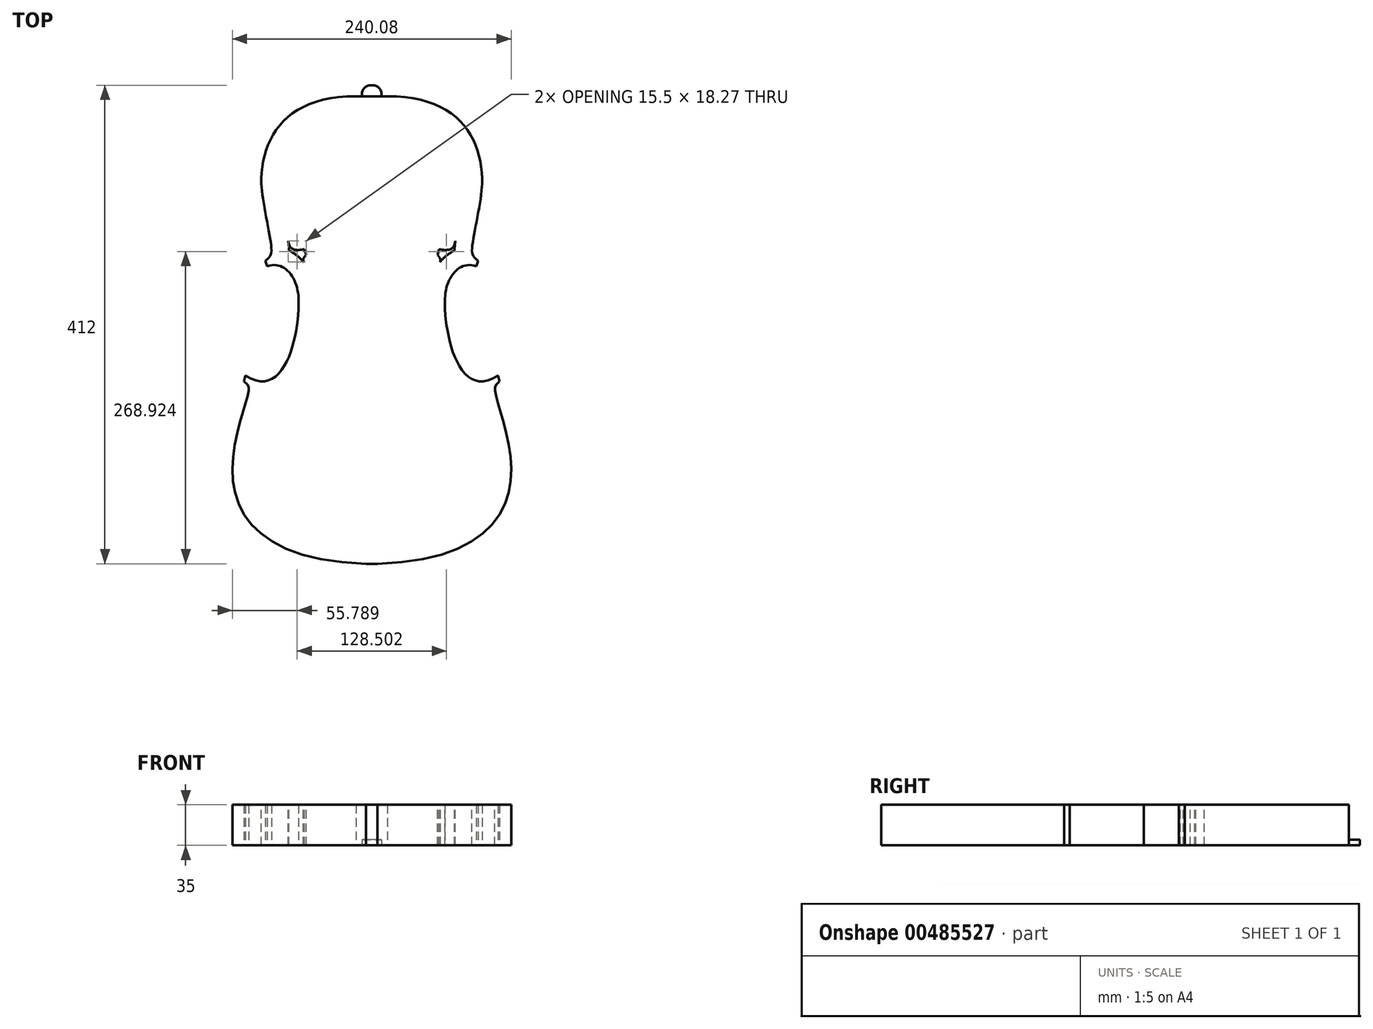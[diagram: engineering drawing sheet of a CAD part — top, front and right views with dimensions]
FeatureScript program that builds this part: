
annotation { "Feature Type Name" : "Feature", "Feature Type Description" : "" }
export const myFeature = defineFeature(function(context is Context, id is Id, definition is map)
    precondition{}
    {
        {
            var Q0;
            Q0=qCreatedBy(makeId("Top.planeOp"),FACE);
            var sketch = newSketch(context, id + "F0", { "sketchPlane" : qUnion([Q0])});
            skLineSegment(sketch, "E0", {"start": v(0, 292.22) * mm, "end": v(-1, 292.22) * mm});
            skLineSegment(sketch, "E1", {"start": v(-1, 292.22) * mm, "end": v(-1, -119.78) * mm});
            skLineSegment(sketch, "E2", {"start": v(12.5, 282.72) * mm, "end": v(7.5, 282.72) * mm});
            skLineSegment(sketch, "E3", {"start": v(7.5, 282.72) * mm, "end": v(7.5, 284.72) * mm});
            skArc(sketch, "E4", {"start": v(7.5, 284.72) * mm, "mid": v(5.3, 290.03) * mm, "end": v(0, 292.22) * mm});
            skFitSpline(sketch, "E5", {"points": [v(94, 207.22) * mm, v(85.5, 153.22) * mm, v(90.5, 141.22) * mm], "startDerivative": vector(-1.32, -59.7) * mm, "endDerivative": vector(44.59, -33.71) * mm});
            skLineSegment(sketch, "E6", {"start": v(90.5, 141.22) * mm, "end": v(89.1, 136.42) * mm});
            skFitSpline(sketch, "E7", {"points": [v(89.1, 136.42) * mm, v(62, 106.22) * mm], "startDerivative": vector(-47.74, 16.25) * mm, "endDerivative": vector(0.93, -57.04) * mm});
            skFitSpline(sketch, "E8", {"points": [v(62, 106.22) * mm, v(107.7, 42.22) * mm], "startDerivative": vector(-1.92, -75.42) * mm, "endDerivative": vector(105.92, 68.08) * mm});
            skLineSegment(sketch, "E9", {"start": v(107.7, 42.22) * mm, "end": v(109, 37.4) * mm});
            skFitSpline(sketch, "E10", {"points": [v(109, 37.4) * mm, v(105, 29.4) * mm, v(119, -41.78) * mm, v(4, -119.78) * mm], "startDerivative": vector(-78.73, -70.42) * mm, "endDerivative": vector(-504.13, -13.55) * mm});
            skLineSegment(sketch, "E11", {"start": v(-1, -119.78) * mm, "end": v(4, -119.78) * mm});
            skFitSpline(sketch, "E12", {"points": [v(94, 207.22) * mm, v(12.5, 282.72) * mm], "startDerivative": vector(2.52, 114) * mm, "endDerivative": vector(-185.72, -1.91) * mm});
            skSolve(sketch);
        }
        {
            var Q0;
            Q0=qSketchRegion(id+"F0",true);
            extrude(context, id + "F1", {"entities" : qUnion([Q0]), "depth" : 35 * mm});
        }
        {
            var Q0;
            Q0=makeQuery(id+"F1.opExtrude","CAP_FACE",FACE,{"disambiguationData":[OSD([sQuery(id+"F0.wireOp",EDGE,"E0"),sQuery(id+"F0.wireOp",EDGE,"E1"),sQuery(id+"F0.wireOp",EDGE,"E2"),sQuery(id+"F0.wireOp",EDGE,"E3"),sQuery(id+"F0.wireOp",EDGE,"E4"),sQuery(id+"F0.wireOp",EDGE,"E5"),sQuery(id+"F0.wireOp",EDGE,"E6"),sQuery(id+"F0.wireOp",EDGE,"E7"),sQuery(id+"F0.wireOp",EDGE,"E8"),sQuery(id+"F0.wireOp",EDGE,"E9"),sQuery(id+"F0.wireOp",EDGE,"E10"),sQuery(id+"F0.wireOp",EDGE,"E11"),sQuery(id+"F0.wireOp",EDGE,"E12")])],"isStart":false});
            var sketch = newSketch(context, id + "F2", { "sketchPlane" : qUnion([Q0])});
            skFitSpline(sketch, "E13.0", {"points": [v(3.6, -104.78) * mm, v(13.6, -104.51) * mm, v(31.77, -103.01) * mm, v(53.82, -98.33) * mm, v(68.13, -92.83) * mm, v(77.37, -87.75) * mm, v(83.29, -83.66) * mm, v(88.28, -79.32) * mm, v(92.44, -74.78) * mm, v(95.87, -70.02) * mm, v(98.64, -65.04) * mm, v(100.82, -59.82) * mm, v(102.44, -54.33) * mm, v(103.33, -49.53) * mm, v(103.78, -45.57) * mm, v(103.98, -42.53) * mm, v(104.06, -39.45) * mm, v(104, -36.28) * mm, v(103.84, -33.05) * mm, v(103.46, -28.68) * mm, v(102.72, -23.13) * mm, v(101.5, -16.45) * mm, v(100.03, -9.86) * mm, v(98.39, -3.45) * mm, v(96.67, 2.69) * mm, v(94.97, 8.47) * mm, v(93.63, 12.95) * mm, v(92.65, 16.33) * mm, v(91.98, 18.76) * mm, v(91.36, 21.1) * mm, v(90.82, 23.4) * mm, v(90.44, 25.32) * mm, v(90.19, 26.92) * mm, v(89.98, 28.6) * mm, v(89.87, 30.47) * mm, v(89.95, 32.6) * mm, v(90.15, 34.32) * mm, v(90.51, 36.12) * mm, v(91.06, 37.93) * mm, v(91.77, 39.67) * mm, v(92.6, 41.27) * mm, v(93.5, 42.69) * mm, v(94.41, 43.91) * mm, v(95.29, 44.95) * mm, v(96.4, 46.15) * mm, v(97.65, 47.35) * mm, v(98.55, 48.17) * mm, v(99, 48.57) * mm]});
            skFitSpline(sketch, "E13.2", {"points": [v(47, 105.98) * mm, v(46.95, 109.13) * mm, v(47.34, 115.34) * mm, v(49.3, 124.25) * mm, v(52.11, 131.2) * mm, v(55.13, 136.4) * mm, v(57.82, 140.07) * mm, v(60.96, 143.47) * mm, v(64.59, 146.5) * mm, v(68.73, 149.07) * mm, v(73.35, 151.03) * mm, v(78.35, 152.24) * mm, v(83.57, 152.6) * mm, v(88.83, 152.09) * mm, v(92.26, 151.2) * mm, v(93.93, 150.62) * mm]});
            skFitSpline(sketch, "E13.3", {"points": [v(81.45, 129.26) * mm, v(80.82, 129.74) * mm, v(79.56, 130.73) * mm, v(77.64, 132.45) * mm, v(75.7, 134.51) * mm, v(73.85, 137.02) * mm, v(72.27, 139.96) * mm, v(71.15, 143.1) * mm, v(70.53, 146.15) * mm, v(70.3, 148.92) * mm, v(70.31, 151.4) * mm, v(70.44, 153.3) * mm, v(70.58, 154.76) * mm, v(70.74, 156.22) * mm, v(70.98, 158.09) * mm, v(71.32, 160.43) * mm, v(71.71, 162.87) * mm, v(72.15, 165.4) * mm, v(72.77, 168.9) * mm, v(73.62, 173.44) * mm, v(74.7, 179.09) * mm, v(75.78, 184.77) * mm, v(76.79, 190.35) * mm, v(77.68, 195.65) * mm, v(78.4, 200.48) * mm, v(78.78, 203.95) * mm, v(78.96, 206.22) * mm, v(79, 207.15) * mm, v(79, 207.55) * mm]});
            skFitSpline(sketch, "E13.4", {"points": [v(79, 207.55) * mm, v(79.1, 211.6) * mm, v(78.7, 219.62) * mm, v(76.7, 229.01) * mm, v(74.2, 235.94) * mm, v(71.84, 240.8) * mm, v(69.02, 245.33) * mm, v(65.7, 249.5) * mm, v(61.85, 253.33) * mm, v(57.37, 256.8) * mm, v(52.2, 259.92) * mm, v(46.23, 262.62) * mm, v(39.38, 264.84) * mm, v(28.96, 267.08) * mm, v(19.62, 267.8) * mm, v(12.65, 267.72) * mm]});
            skFitSpline(sketch, "E13.5", {"points": [v(115.81, 29.6) * mm, v(114.35, 28.66) * mm, v(111.4, 26.94) * mm, v(106.84, 24.86) * mm, v(102.17, 23.33) * mm, v(97.36, 22.42) * mm, v(92.5, 22.18) * mm, v(87.7, 22.66) * mm, v(83.1, 23.82) * mm, v(78.84, 25.6) * mm, v(74.98, 27.85) * mm, v(71.54, 30.48) * mm, v(68.5, 33.37) * mm, v(64.9, 37.49) * mm, v(61.18, 43.02) * mm, v(57.59, 50.06) * mm, v(54.68, 57.4) * mm, v(52.34, 64.9) * mm, v(50.48, 72.48) * mm, v(49.05, 79.99) * mm, v(48, 87.3) * mm, v(47.32, 94.26) * mm, v(46.97, 100.76) * mm, v(46.96, 104.72) * mm, v(47, 106.6) * mm]});
            skFitSpline(sketch, "E14", {"points": [v(39, 264.81) * mm, v(14, 163.36) * mm, v(83.4, -83.4) * mm], "startDerivative": vector(-160.07, 44.9) * mm, "endDerivative": vector(195.96, 107.88) * mm});
            skLineSegment(sketch, "E15.0", {"start": v(56.9, 151.02) * mm, "end": v(55.5, 146.22) * mm});
            skFitSpline(sketch, "E16", {"points": [v(56.9, 151.02) * mm, v(71.03, 158.45) * mm], "startDerivative": vector(34.35, -6.8) * mm, "endDerivative": vector(3.02, 16.74) * mm});
            skFitSpline(sketch, "E17", {"points": [v(55.5, 146.22) * mm, v(57.47, 139.5) * mm], "startDerivative": vector(5.3, -4.74) * mm, "endDerivative": vector(-4.61, -6.5) * mm});
            skLineSegment(sketch, "E18", {"start": v(90.5, 141.22) * mm, "end": v(56.9, 151.02) * mm, "construction": true});
            skLineSegment(sketch, "E19", {"start": v(55.5, 146.22) * mm, "end": v(89.1, 136.42) * mm, "construction": true});
            skLineSegment(sketch, "E20.0", {"start": v(78.85, 17.01) * mm, "end": v(80.48, 10.95) * mm});
            skLineSegment(sketch, "E21", {"start": v(107.7, 42.22) * mm, "end": v(78.85, 17.01) * mm, "construction": true});
            skLineSegment(sketch, "E22", {"start": v(109, 37.4) * mm, "end": v(80.48, 10.95) * mm, "construction": true});
            skFitSpline(sketch, "E23", {"points": [v(78.85, 17.01) * mm, v(71.97, 30.22) * mm], "startDerivative": vector(14.22, 16.83) * mm, "endDerivative": vector(-19.83, 18.83) * mm});
            skFitSpline(sketch, "E24", {"points": [v(80.48, 10.95) * mm, v(95.87, 5.38) * mm], "startDerivative": vector(20.38, 9.74) * mm, "endDerivative": vector(7.24, -17.6) * mm});
            skSolve(sketch);
        }
        {
            var Q0;
            Q0=qCreatedBy(makeId("Front.planeOp"),FACE);
            cPlane(context, id + "F3", {"entities" : qUnion([Q0]), "cplaneType" : CPlaneType.OFFSET, "offset" : 95 * mm, "oppositeDirection" : true, "width" : 150 * mm, "height" : 150 * mm});
        }
        {
            var Q0;
            Q0=qSketchRegion(id+"F2",true);
            extrude(context, id + "F4", {"entities" : qUnion([Q0]), "operationType" : NewBodyOperationType.REMOVE, "endBound" : BoundingType.THROUGH_ALL, "oppositeDirection" : true, "depth" : 25 * mm});
        }
        {
            var Q0;
            Q0=qCreatedBy(id+"F3.planeOp",FACE);
            var sketch = newSketch(context, id + "F5", { "sketchPlane" : qUnion([Q0])});
            skLineSegment(sketch, "E25", {"start": v(0, 0) * mm, "end": v(0, 35) * mm, "construction": true});
            skLineSegment(sketch, "E26", {"start": v(120.4, 25) * mm, "end": v(120.4, 5) * mm, "construction": true});
            skLineSegment(sketch, "E27", {"start": v(0, 35) * mm, "end": v(11.56, 35) * mm});
            skLineSegment(sketch, "E28", {"start": v(0, 0) * mm, "end": v(18.73, 0) * mm});
            skFitSpline(sketch, "E29", {"points": [v(11.56, 35) * mm, v(120.4, 25) * mm], "startDerivative": vector(190.4, 0.48) * mm, "endDerivative": vector(73.97, -18.77) * mm});
            skFitSpline(sketch, "E30", {"points": [v(120.4, 5) * mm, v(18.73, 0) * mm], "startDerivative": vector(-51.91, -7) * mm, "endDerivative": vector(-188.2, -0.12) * mm});
            skLineSegment(sketch, "E31", {"start": v(0, 35) * mm, "end": v(-9.35, 35) * mm});
            skLineSegment(sketch, "E32", {"start": v(-9.35, 35) * mm, "end": v(-9.35, 48.37) * mm});
            skLineSegment(sketch, "E33", {"start": v(-9.35, 48.37) * mm, "end": v(121.24, 48.37) * mm});
            skLineSegment(sketch, "E34", {"start": v(121.24, 48.37) * mm, "end": v(120.4, 25) * mm});
            skLineSegment(sketch, "E35", {"start": v(120.4, 5) * mm, "end": v(120.4, -6.45) * mm});
            skLineSegment(sketch, "E36", {"start": v(120.4, -6.45) * mm, "end": v(0, -7.07) * mm});
            skLineSegment(sketch, "E37", {"start": v(0, -7.07) * mm, "end": v(0, 0) * mm});
            skSolve(sketch);
        }
        {
            var Q0;
            Q0=makeQuery(id+"F1.opExtrude","SWEPT_BODY",BODY,{"disambiguationData":[OSD([sQuery(id+"F0.wireOp",EDGE,"E0"),sQuery(id+"F0.wireOp",EDGE,"E1"),sQuery(id+"F0.wireOp",EDGE,"E2"),sQuery(id+"F0.wireOp",EDGE,"E3"),sQuery(id+"F0.wireOp",EDGE,"E4"),sQuery(id+"F0.wireOp",EDGE,"E5"),sQuery(id+"F0.wireOp",EDGE,"E6"),sQuery(id+"F0.wireOp",EDGE,"E7"),sQuery(id+"F0.wireOp",EDGE,"E8"),sQuery(id+"F0.wireOp",EDGE,"E9"),sQuery(id+"F0.wireOp",EDGE,"E10"),sQuery(id+"F0.wireOp",EDGE,"E11"),sQuery(id+"F0.wireOp",EDGE,"E12")])]});
            var Q1;
            Q1=makeQuery(id+"F1.opExtrude","SWEPT_FACE",FACE,{"disambiguationData":[OSD([sQuery(id+"F0.wireOp",EDGE,"E1")])]});
            mirror(context, id + "F6", {"operationType" : NewBodyOperationType.ADD, "entities" : qUnion([Q0]), "mirrorPlane" : qUnion([Q1])});
        }
        {
            var Q0;
            {var subQ0=makeQuery(id+"F1.opExtrude","CAP_FACE",FACE,{"disambiguationData":[OSD([sQuery(id+"F0.wireOp",EDGE,"E0"),sQuery(id+"F0.wireOp",EDGE,"E1"),sQuery(id+"F0.wireOp",EDGE,"E2"),sQuery(id+"F0.wireOp",EDGE,"E3"),sQuery(id+"F0.wireOp",EDGE,"E4"),sQuery(id+"F0.wireOp",EDGE,"E5"),sQuery(id+"F0.wireOp",EDGE,"E6"),sQuery(id+"F0.wireOp",EDGE,"E7"),sQuery(id+"F0.wireOp",EDGE,"E8"),sQuery(id+"F0.wireOp",EDGE,"E9"),sQuery(id+"F0.wireOp",EDGE,"E10"),sQuery(id+"F0.wireOp",EDGE,"E11"),sQuery(id+"F0.wireOp",EDGE,"E12")])],"isStart":false});Q0=makeQuery(id+"F6.boolean.opBoolean","MERGE",FACE,{"derivedFrom":[subQ0,makeQuery(id+"F6.opPattern","COPY",FACE,{"derivedFrom":subQ0,"instanceName":"1"})]});}
            var sketch = newSketch(context, id + "F7", { "sketchPlane" : qUnion([Q0])});
            skLineSegment(sketch, "E38.bottom", {"start": v(-9.5, 282.72) * mm, "end": v(7.5, 282.72) * mm});
            skLineSegment(sketch, "E38.top", {"start": v(-9.5, 294.99) * mm, "end": v(7.5, 294.99) * mm});
            skLineSegment(sketch, "E38.left", {"start": v(-9.5, 282.72) * mm, "end": v(-9.5, 294.99) * mm});
            skLineSegment(sketch, "E38.right", {"start": v(7.5, 282.72) * mm, "end": v(7.5, 294.99) * mm});
            skSolve(sketch);
        }
        {
            var Q0;
            Q0=qSketchRegion(id+"F7",true);
            extrude(context, id + "F8", {"entities" : qUnion([Q0]), "operationType" : NewBodyOperationType.REMOVE, "oppositeDirection" : true, "depth" : 30 * mm});
        }
    });
